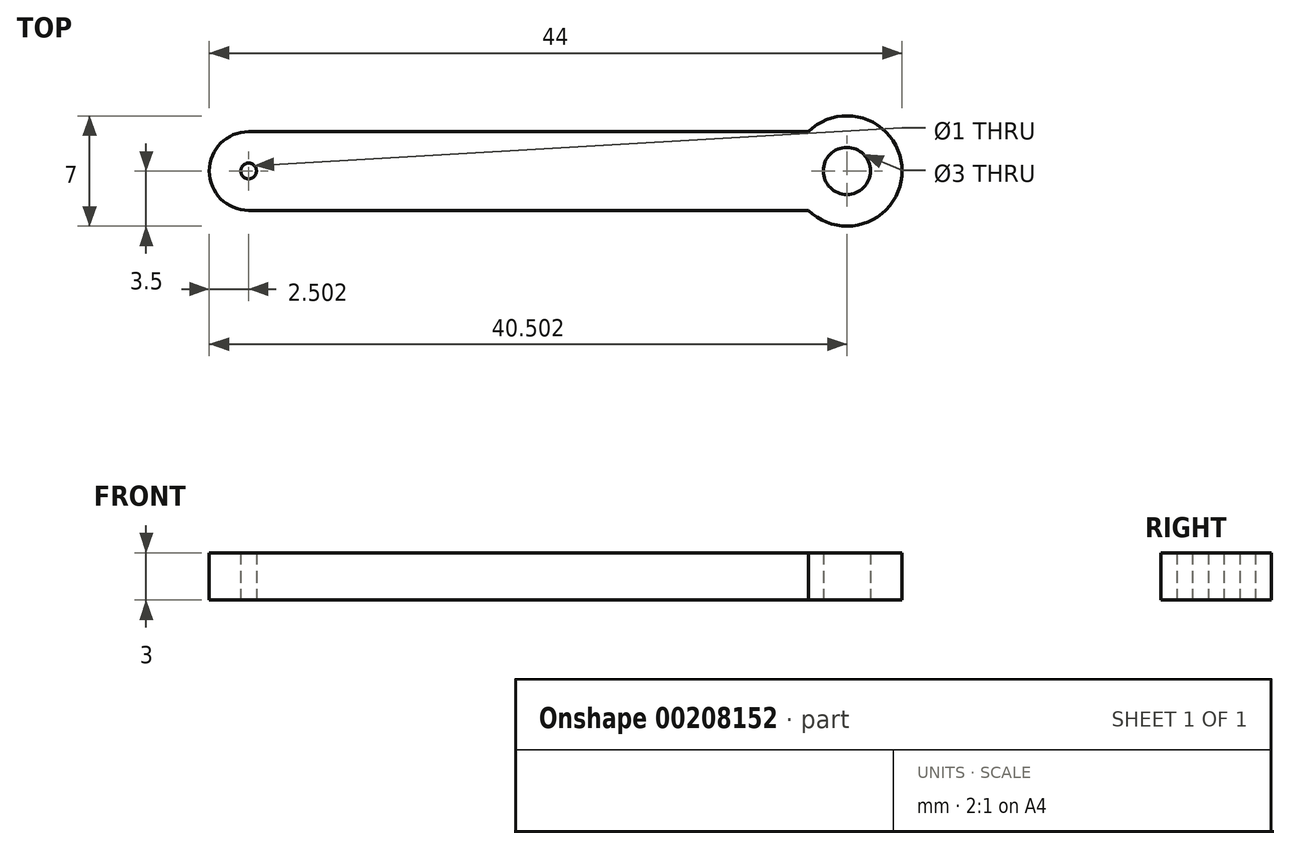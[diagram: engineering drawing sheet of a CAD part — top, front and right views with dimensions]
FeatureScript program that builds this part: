
annotation { "Feature Type Name" : "Feature", "Feature Type Description" : "" }
export const myFeature = defineFeature(function(context is Context, id is Id, definition is map)
    precondition{}
    {
        {
            var Q0;
            Q0=qCreatedBy(makeId("Top.planeOp"),FACE);
            var sketch = newSketch(context, id + "F0", { "sketchPlane" : qUnion([Q0])});
            skCircle(sketch, "E0", {"center": v(-9.84, 0) * mm, "radius": 0.5 * mm});
            skCircle(sketch, "E1", {"center": v(28.16, 0) * mm, "radius": 1.5 * mm});
            skLineSegment(sketch, "E2", {"start": v(25.71, 2.5) * mm, "end": v(-9.84, 2.5) * mm});
            skLineSegment(sketch, "E3", {"start": v(-9.84, -2.5) * mm, "end": v(25.71, -2.5) * mm});
            skArc(sketch, "E4", {"start": v(-9.84, 2.5) * mm, "mid": v(-12.34, 0) * mm, "end": v(-9.84, -2.5) * mm});
            skArc(sketch, "E5", {"start": v(25.71, -2.5) * mm, "mid": v(31.66, 0) * mm, "end": v(25.71, 2.5) * mm});
            skSolve(sketch);
        }
        {
            var Q0;
            Q0=makeQuery(id+"F0.imprint","IMPRINT",FACE,{"disambiguationData":[TD([[makeQuery(id+"F0.imprint","IMPRINT",EDGE,{"derivedFrom":sQuery(id+"F0.wireOp",EDGE,"E0")}),-1.0]])]});
            extrude(context, id + "F1", {"entities" : qUnion([Q0]), "depth" : 3 * mm});
        }
    });
